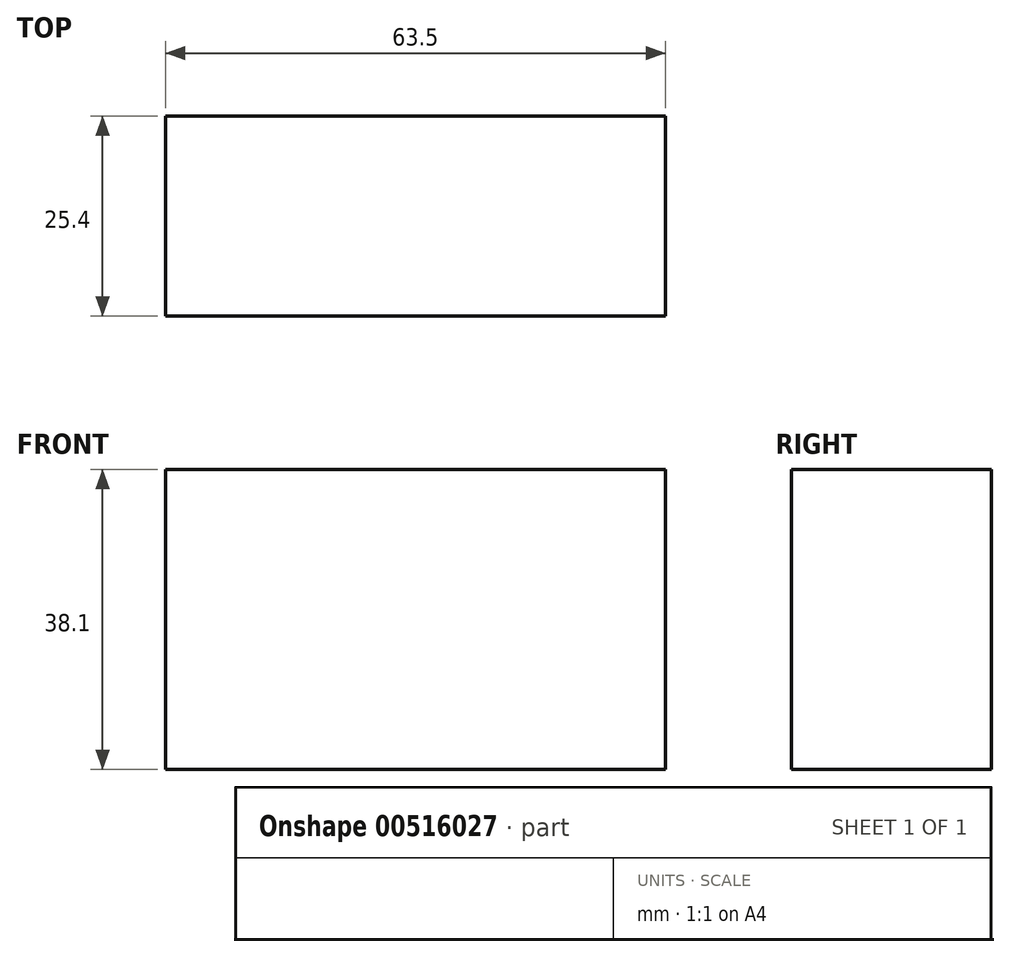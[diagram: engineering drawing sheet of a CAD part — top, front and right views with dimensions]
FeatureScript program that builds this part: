
annotation { "Feature Type Name" : "Feature", "Feature Type Description" : "" }
export const myFeature = defineFeature(function(context is Context, id is Id, definition is map)
    precondition{}
    {
        {
            var Q0;
            Q0=qCreatedBy(makeId("Front.planeOp"),FACE);
            var sketch = newSketch(context, id + "F0", { "sketchPlane" : qUnion([Q0])});
            skLineSegment(sketch, "E0.bottom", {"start": v(-26.36, 18.37) * mm, "end": v(37.14, 18.37) * mm});
            skLineSegment(sketch, "E0.top", {"start": v(-26.36, -19.73) * mm, "end": v(37.14, -19.73) * mm});
            skLineSegment(sketch, "E0.left", {"start": v(-26.36, 18.37) * mm, "end": v(-26.36, -19.73) * mm});
            skLineSegment(sketch, "E0.right", {"start": v(37.14, 18.37) * mm, "end": v(37.14, -19.73) * mm});
            skSolve(sketch);
        }
        {
            var Q0;
            Q0=makeQuery(id+"F0.imprint","IMPRINT",FACE,{"disambiguationData":[TD([[makeQuery(id+"F0.imprint","IMPRINT",EDGE,{"derivedFrom":sQuery(id+"F0.wireOp",EDGE,"E0.bottom")}),-1.0]])]});
            extrude(context, id + "F1", {"entities" : qUnion([Q0]), "depth" : 25.4 * mm, "offsetDistance" : 25.4 * mm});
        }
    });
